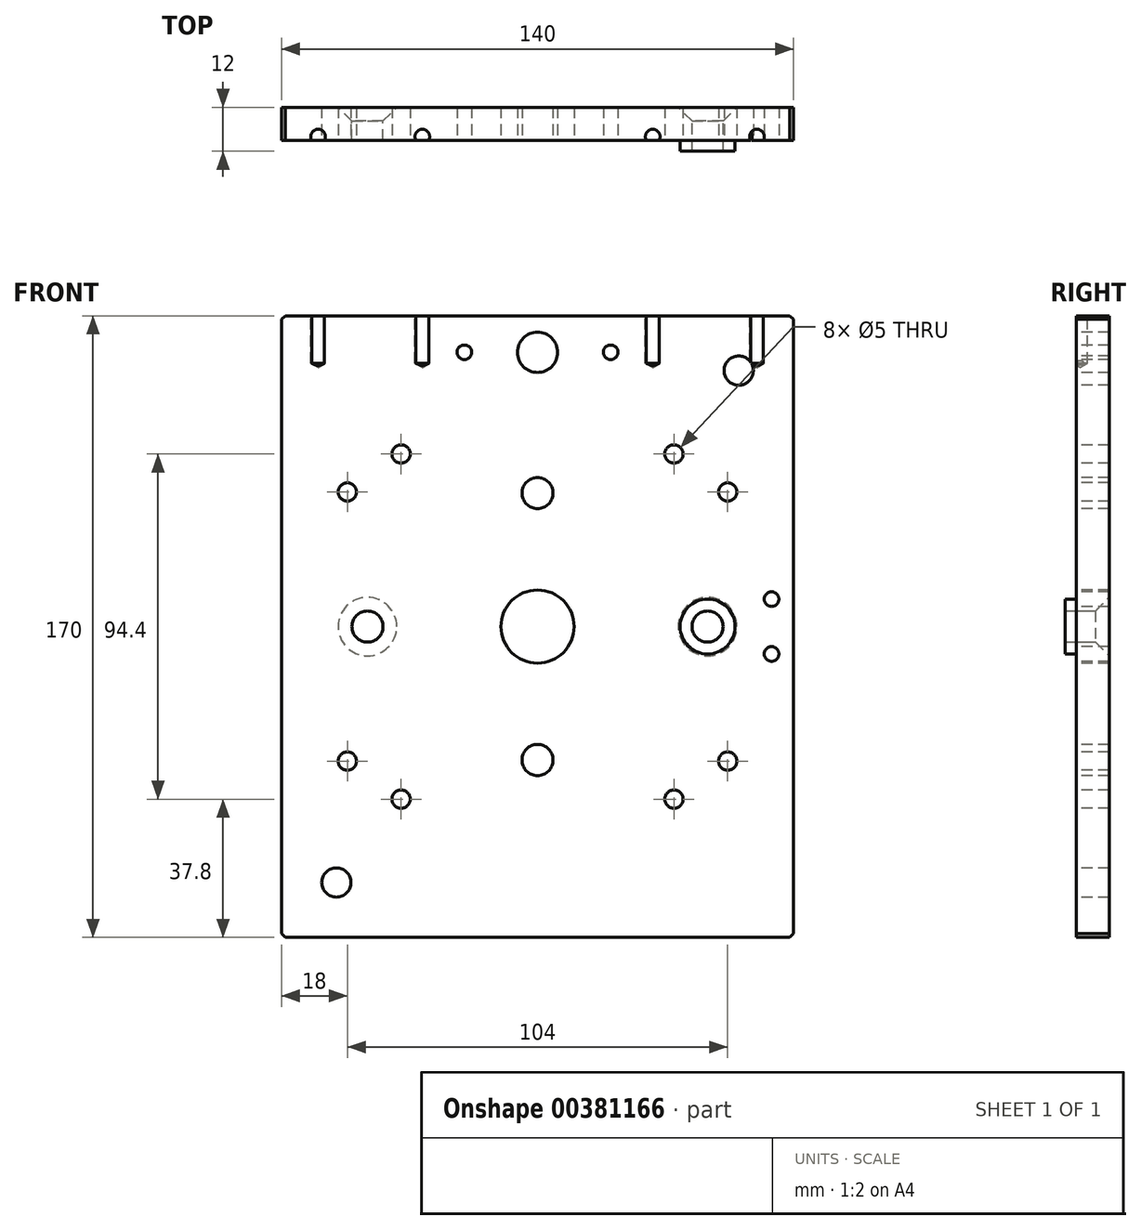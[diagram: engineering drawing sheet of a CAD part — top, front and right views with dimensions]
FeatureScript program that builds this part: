
annotation { "Feature Type Name" : "Feature", "Feature Type Description" : "" }
export const myFeature = defineFeature(function(context is Context, id is Id, definition is map)
    precondition{}
    {
        {
            var Q0;
            Q0=qCreatedBy(makeId("Front.planeOp"),FACE);
            var sketch = newSketch(context, id + "F0", { "sketchPlane" : qUnion([Q0])});
            skLineSegment(sketch, "E0.bottom", {"start": v(-70, -85) * mm, "end": v(70, -85) * mm});
            skLineSegment(sketch, "E0.top", {"start": v(-70, 85) * mm, "end": v(70, 85) * mm});
            skLineSegment(sketch, "E0.left", {"start": v(-70, -85) * mm, "end": v(-70, 85) * mm});
            skLineSegment(sketch, "E0.right", {"start": v(70, -85) * mm, "end": v(70, 85) * mm});
            skSolve(sketch);
        }
        {
            var Q0;
            Q0=makeQuery(id+"F0.imprint","IMPRINT",FACE,{"disambiguationData":[TD([[makeQuery(id+"F0.imprint","IMPRINT",EDGE,{"derivedFrom":sQuery(id+"F0.wireOp",EDGE,"E0.bottom")}),1.0]])]});
            extrude(context, id + "F1", {"entities" : qUnion([Q0]), "depth" : 12 * mm});
        }
        {
            var Q0;
            Q0=makeQuery(id+"F1.opExtrude","CAP_FACE",FACE,{"disambiguationData":[OSD([sQuery(id+"F0.wireOp",EDGE,"E0.bottom"),sQuery(id+"F0.wireOp",EDGE,"E0.top"),sQuery(id+"F0.wireOp",EDGE,"E0.left"),sQuery(id+"F0.wireOp",EDGE,"E0.right")])],"isStart":false});
            var sketch = newSketch(context, id + "F2", { "sketchPlane" : qUnion([Q0])});
            skCircle(sketch, "E1", {"center": v(0, 0) * mm, "radius": 10 * mm});
            skSolve(sketch);
        }
        {
            var Q0;
            Q0=makeQuery(id+"F2.imprint","IMPRINT",FACE,{"disambiguationData":[TD([[makeQuery(id+"F2.imprint","IMPRINT",EDGE,{"derivedFrom":sQuery(id+"F2.wireOp",EDGE,"E1")}),1.0]])]});
            extrude(context, id + "F3", {"entities" : qUnion([Q0]), "operationType" : NewBodyOperationType.REMOVE, "oppositeDirection" : true, "depth" : 12 * mm});
        }
        {
            var Q0;
            Q0=makeQuery(id+"F1.opExtrude","CAP_FACE",FACE,{"disambiguationData":[OSD([sQuery(id+"F0.wireOp",EDGE,"E0.bottom"),sQuery(id+"F0.wireOp",EDGE,"E0.top"),sQuery(id+"F0.wireOp",EDGE,"E0.left"),sQuery(id+"F0.wireOp",EDGE,"E0.right")])],"isStart":false});
            var sketch = newSketch(context, id + "F4", { "sketchPlane" : qUnion([Q0])});
            skPoint(sketch, "E2", {"position": v(-55, -70) * mm});
            skPoint(sketch, "E3", {"position": v(55, 70) * mm});
            skSolve(sketch);
        }
        {
            var Q0;
            Q0=sQuery(id+"F4.wireOp",VERTEX,"E2");
            var Q1;
            Q1=sQuery(id+"F4.wireOp",VERTEX,"E3");
            var Q2;
            Q2=makeQuery(id+"F1.opExtrude","SWEPT_BODY",BODY,{"disambiguationData":[OSD([sQuery(id+"F0.wireOp",EDGE,"E0.bottom"),sQuery(id+"F0.wireOp",EDGE,"E0.top"),sQuery(id+"F0.wireOp",EDGE,"E0.left"),sQuery(id+"F0.wireOp",EDGE,"E0.right")])]});
            hole(context, id + "F5", {"style" : HoleStyle.SIMPLE, "endStyle" : HoleEndStyle.THROUGH, "holeDiameter" : 8 * mm, "isTappedThrough" : true, "tappedDepth" : 12 * mm, "tapClearance" : 3, "locations" : qUnion([Q0, Q1]), "scope" : qUnion([Q2])});
        }
        {
            var Q0;
            Q0=makeQuery(id+"F1.opExtrude","CAP_FACE",FACE,{"disambiguationData":[OSD([sQuery(id+"F0.wireOp",EDGE,"E0.bottom"),sQuery(id+"F0.wireOp",EDGE,"E0.top"),sQuery(id+"F0.wireOp",EDGE,"E0.left"),sQuery(id+"F0.wireOp",EDGE,"E0.right")])],"isStart":false});
            var sketch = newSketch(context, id + "F6", { "sketchPlane" : qUnion([Q0])});
            skCircle(sketch, "E4", {"center": v(-46.5, 0) * mm, "radius": 7.5 * mm});
            skCircle(sketch, "E5.MirrorC", {"center": v(46.5, 0) * mm, "radius": 7.5 * mm});
            skSolve(sketch);
        }
        {
            var Q0;
            Q0=makeQuery(id+"F6.imprint","IMPRINT",FACE,{"disambiguationData":[TD([[makeQuery(id+"F6.imprint","IMPRINT",EDGE,{"derivedFrom":sQuery(id+"F6.wireOp",EDGE,"E4")}),1.0]])]});
            var Q1;
            Q1=makeQuery(id+"F6.imprint","IMPRINT",FACE,{"disambiguationData":[TD([[makeQuery(id+"F6.imprint","IMPRINT",EDGE,{"derivedFrom":sQuery(id+"F6.wireOp",EDGE,"E5.MirrorC")}),-1.0]])]});
            extrude(context, id + "F7", {"entities" : qUnion([Q0, Q1]), "operationType" : NewBodyOperationType.REMOVE, "oppositeDirection" : true, "depth" : 3 * mm});
        }
        {
            var Q0;
            Q0=makeQuery(id+"F1.opExtrude","CAP_FACE",FACE,{"disambiguationData":[OSD([sQuery(id+"F0.wireOp",EDGE,"E0.bottom"),sQuery(id+"F0.wireOp",EDGE,"E0.top"),sQuery(id+"F0.wireOp",EDGE,"E0.left"),sQuery(id+"F0.wireOp",EDGE,"E0.right")])],"isStart":true});
            var sketch = newSketch(context, id + "F8", { "sketchPlane" : qUnion([Q0])});
            skPoint(sketch, "E6", {"position": v(46.5, 0) * mm});
            skPoint(sketch, "E7.MirrorP", {"position": v(-46.5, 0) * mm});
            skSolve(sketch);
        }
        {
            var Q0;
            Q0=sQuery(id+"F8.wireOp",VERTEX,"E6");
            var Q1;
            Q1=sQuery(id+"F8.wireOp",VERTEX,"E7.MirrorP");
            var Q2;
            Q2=makeQuery(id+"F1.opExtrude","SWEPT_BODY",BODY,{"disambiguationData":[OSD([sQuery(id+"F0.wireOp",EDGE,"E0.bottom"),sQuery(id+"F0.wireOp",EDGE,"E0.top"),sQuery(id+"F0.wireOp",EDGE,"E0.left"),sQuery(id+"F0.wireOp",EDGE,"E0.right")])]});
            hole(context, id + "F9", {"style" : HoleStyle.C_SINK, "endStyle" : HoleEndStyle.BLIND, "holeDiameter" : 8.5 * mm, "cSinkDiameter" : 16 * mm, "cSinkAngle" : 90 * degree, "holeDepth" : 12 * mm, "isTappedThrough" : true, "tappedDepth" : 12 * mm, "tapClearance" : 3, "locations" : qUnion([Q0, Q1]), "scope" : qUnion([Q2])});
        }
        {
            var Q0;
            Q0=makeQuery(id+"F1.opExtrude","CAP_FACE",FACE,{"disambiguationData":[OSD([sQuery(id+"F0.wireOp",EDGE,"E0.bottom"),sQuery(id+"F0.wireOp",EDGE,"E0.top"),sQuery(id+"F0.wireOp",EDGE,"E0.left"),sQuery(id+"F0.wireOp",EDGE,"E0.right")])],"isStart":false});
            var sketch = newSketch(context, id + "F10", { "sketchPlane" : qUnion([Q0])});
            skPoint(sketch, "E8", {"position": v(0, -36.5) * mm});
            skPoint(sketch, "E9.MirrorP", {"position": v(0, 36.5) * mm});
            skSolve(sketch);
        }
        {
            var Q0;
            Q0=sQuery(id+"F10.wireOp",VERTEX,"E8");
            var Q1;
            Q1=sQuery(id+"F10.wireOp",VERTEX,"E9.MirrorP");
            var Q2;
            Q2=makeQuery(id+"F1.opExtrude","SWEPT_BODY",BODY,{"disambiguationData":[OSD([sQuery(id+"F0.wireOp",EDGE,"E0.bottom"),sQuery(id+"F0.wireOp",EDGE,"E0.top"),sQuery(id+"F0.wireOp",EDGE,"E0.left"),sQuery(id+"F0.wireOp",EDGE,"E0.right")])]});
            hole(context, id + "F11", {"style" : HoleStyle.SIMPLE, "endStyle" : HoleEndStyle.THROUGH, "standardTappedOrClearance" : lookupTablePath({ "standard" : "ISO", "engagement" : "75%", "pitch" : "1.5 mm", "size" : "M10", "type" : "Tapped" }), "standardBlindInLast" : lookupTablePath({ "standard" : "ISO", "engagement" : "75%", "pitch" : "1.5 mm", "size" : "M10", "type" : "Tapped" }), "holeDiameter" : 8.5 * mm, "showTappedDepth" : true, "isTappedThrough" : true, "tappedDepth" : 12 * mm, "tapClearance" : 3, "locations" : qUnion([Q0, Q1]), "scope" : qUnion([Q2]), "majorDiameter" : 10 * mm});
        }
        {
            var Q0;
            Q0=makeQuery(id+"F1.opExtrude","CAP_FACE",FACE,{"disambiguationData":[OSD([sQuery(id+"F0.wireOp",EDGE,"E0.bottom"),sQuery(id+"F0.wireOp",EDGE,"E0.top"),sQuery(id+"F0.wireOp",EDGE,"E0.left"),sQuery(id+"F0.wireOp",EDGE,"E0.right")])],"isStart":false});
            var sketch = newSketch(context, id + "F12", { "sketchPlane" : qUnion([Q0])});
            skPoint(sketch, "E10", {"position": v(-52, 36.8) * mm});
            skPoint(sketch, "E11", {"position": v(-37.3, 47.2) * mm});
            skPoint(sketch, "E12.MirrorP", {"position": v(52, 36.8) * mm});
            skPoint(sketch, "E13.MirrorP", {"position": v(37.3, 47.2) * mm});
            skPoint(sketch, "E14.MirrorP", {"position": v(52, -36.8) * mm});
            skPoint(sketch, "E15.MirrorP", {"position": v(37.3, -47.2) * mm});
            skPoint(sketch, "E16.MirrorP", {"position": v(-37.3, -47.2) * mm});
            skPoint(sketch, "E17.MirrorP", {"position": v(-52, -36.8) * mm});
            skSolve(sketch);
        }
        {
            var Q0;
            Q0=sQuery(id+"F12.wireOp",VERTEX,"E14.MirrorP");
            var Q1;
            Q1=sQuery(id+"F12.wireOp",VERTEX,"E15.MirrorP");
            var Q2;
            Q2=sQuery(id+"F12.wireOp",VERTEX,"E16.MirrorP");
            var Q3;
            Q3=sQuery(id+"F12.wireOp",VERTEX,"E17.MirrorP");
            var Q4;
            Q4=sQuery(id+"F12.wireOp",VERTEX,"E10");
            var Q5;
            Q5=sQuery(id+"F12.wireOp",VERTEX,"E11");
            var Q6;
            Q6=sQuery(id+"F12.wireOp",VERTEX,"E13.MirrorP");
            var Q7;
            Q7=sQuery(id+"F12.wireOp",VERTEX,"E12.MirrorP");
            var Q8;
            Q8=makeQuery(id+"F1.opExtrude","SWEPT_BODY",BODY,{"disambiguationData":[OSD([sQuery(id+"F0.wireOp",EDGE,"E0.bottom"),sQuery(id+"F0.wireOp",EDGE,"E0.top"),sQuery(id+"F0.wireOp",EDGE,"E0.left"),sQuery(id+"F0.wireOp",EDGE,"E0.right")])]});
            hole(context, id + "F13", {"style" : HoleStyle.SIMPLE, "endStyle" : HoleEndStyle.THROUGH, "standardTappedOrClearance" : lookupTablePath({ "standard" : "ISO", "engagement" : "75%", "pitch" : "1 mm", "size" : "M6", "type" : "Tapped" }), "standardBlindInLast" : lookupTablePath({ "standard" : "ISO", "engagement" : "75%", "pitch" : "1 mm", "size" : "M6", "type" : "Tapped" }), "holeDiameter" : 5 * mm, "showTappedDepth" : true, "isTappedThrough" : true, "tappedDepth" : 12 * mm, "tapClearance" : 3, "locations" : qUnion([Q0, Q1, Q2, Q3, Q4, Q5, Q6, Q7]), "scope" : qUnion([Q8]), "majorDiameter" : 6 * mm});
        }
        {
            var Q0;
            Q0=makeQuery(id+"F1.opExtrude","CAP_FACE",FACE,{"disambiguationData":[OSD([sQuery(id+"F0.wireOp",EDGE,"E0.bottom"),sQuery(id+"F0.wireOp",EDGE,"E0.top"),sQuery(id+"F0.wireOp",EDGE,"E0.left"),sQuery(id+"F0.wireOp",EDGE,"E0.right")])],"isStart":false});
            var sketch = newSketch(context, id + "F14", { "sketchPlane" : qUnion([Q0])});
            skPoint(sketch, "E18", {"position": v(64, -7.5) * mm});
            skPoint(sketch, "E19.MirrorP", {"position": v(64, 7.5) * mm});
            skPoint(sketch, "E20", {"position": v(-20, 75) * mm});
            skPoint(sketch, "E21.MirrorP", {"position": v(20, 75) * mm});
            skSolve(sketch);
        }
        {
            var Q0;
            Q0=sQuery(id+"F14.wireOp",VERTEX,"E20");
            var Q1;
            Q1=sQuery(id+"F14.wireOp",VERTEX,"E21.MirrorP");
            var Q2;
            Q2=sQuery(id+"F14.wireOp",VERTEX,"E19.MirrorP");
            var Q3;
            Q3=sQuery(id+"F14.wireOp",VERTEX,"E18");
            var Q4;
            Q4=makeQuery(id+"F1.opExtrude","SWEPT_BODY",BODY,{"disambiguationData":[OSD([sQuery(id+"F0.wireOp",EDGE,"E0.bottom"),sQuery(id+"F0.wireOp",EDGE,"E0.top"),sQuery(id+"F0.wireOp",EDGE,"E0.left"),sQuery(id+"F0.wireOp",EDGE,"E0.right")])]});
            hole(context, id + "F15", {"style" : HoleStyle.SIMPLE, "endStyle" : HoleEndStyle.THROUGH, "standardTappedOrClearance" : lookupTablePath({ "standard" : "ISO", "engagement" : "75%", "pitch" : "1 mm", "size" : "M5", "type" : "Tapped" }), "standardBlindInLast" : lookupTablePath({ "standard" : "ISO", "engagement" : "75%", "pitch" : "1 mm", "size" : "M5", "type" : "Tapped" }), "holeDiameter" : 4 * mm, "showTappedDepth" : true, "isTappedThrough" : true, "tappedDepth" : 12 * mm, "tapClearance" : 3, "locations" : qUnion([Q0, Q1, Q2, Q3]), "scope" : qUnion([Q4])});
        }
        {
            var Q0;
            Q0=makeQuery(id+"F1.opExtrude","CAP_FACE",FACE,{"disambiguationData":[OSD([sQuery(id+"F0.wireOp",EDGE,"E0.bottom"),sQuery(id+"F0.wireOp",EDGE,"E0.top"),sQuery(id+"F0.wireOp",EDGE,"E0.left"),sQuery(id+"F0.wireOp",EDGE,"E0.right")])],"isStart":false});
            var sketch = newSketch(context, id + "F16", { "sketchPlane" : qUnion([Q0])});
            skCircle(sketch, "E22", {"center": v(0, 75) * mm, "radius": 5.5 * mm});
            skSolve(sketch);
        }
        {
            var Q0;
            Q0=makeQuery(id+"F16.imprint","IMPRINT",FACE,{"disambiguationData":[TD([[makeQuery(id+"F16.imprint","IMPRINT",EDGE,{"derivedFrom":sQuery(id+"F16.wireOp",EDGE,"E22")}),1.0]])]});
            extrude(context, id + "F17", {"entities" : qUnion([Q0]), "operationType" : NewBodyOperationType.REMOVE, "oppositeDirection" : true, "depth" : 12 * mm});
        }
        {
            var Q0;
            Q0=makeQuery(id+"F1.opExtrude","SWEPT_FACE",FACE,{"disambiguationData":[OSD([sQuery(id+"F0.wireOp",EDGE,"E0.top")])]});
            var sketch = newSketch(context, id + "F18", { "sketchPlane" : qUnion([Q0])});
            skPoint(sketch, "E23", {"position": v(60, -8) * mm});
            skPoint(sketch, "E24", {"position": v(31.5, -8) * mm});
            skPoint(sketch, "E25.MirrorP", {"position": v(-31.5, -8) * mm});
            skPoint(sketch, "E26.MirrorP", {"position": v(-60, -8) * mm});
            skSolve(sketch);
        }
        {
            var Q0;
            Q0=sQuery(id+"F18.wireOp",VERTEX,"E23");
            var Q1;
            Q1=sQuery(id+"F18.wireOp",VERTEX,"E24");
            var Q2;
            Q2=sQuery(id+"F18.wireOp",VERTEX,"E25.MirrorP");
            var Q3;
            Q3=sQuery(id+"F18.wireOp",VERTEX,"E26.MirrorP");
            var Q4;
            Q4=makeQuery(id+"F1.opExtrude","SWEPT_BODY",BODY,{"disambiguationData":[OSD([sQuery(id+"F0.wireOp",EDGE,"E0.bottom"),sQuery(id+"F0.wireOp",EDGE,"E0.top"),sQuery(id+"F0.wireOp",EDGE,"E0.left"),sQuery(id+"F0.wireOp",EDGE,"E0.right")])]});
            hole(context, id + "F19", {"style" : HoleStyle.SIMPLE, "endStyle" : HoleEndStyle.BLIND, "standardTappedOrClearance" : lookupTablePath({ "standard" : "ISO", "engagement" : "75%", "pitch" : "1 mm", "size" : "M5", "type" : "Tapped" }), "standardBlindInLast" : lookupTablePath({ "standard" : "ISO", "engagement" : "75%", "pitch" : "1 mm", "size" : "M5", "type" : "Tapped" }), "holeDiameter" : 4 * mm, "showTappedDepth" : true, "holeDepth" : 13 * mm, "isTappedThrough" : true, "tappedDepth" : 10 * mm, "tapClearance" : 3, "locations" : qUnion([Q0, Q1, Q2, Q3]), "scope" : qUnion([Q4])});
        }
        {
            var Q0;
            Q0=makeQuery(id+"F1.opExtrude","SWEPT_EDGE",EDGE,{"disambiguationData":[OSD([sQuery(id+"F0.wireOp",EDGE,"E0.bottom"),sQuery(id+"F0.wireOp",EDGE,"E0.left")])]});
            var Q1;
            Q1=makeQuery(id+"F1.opExtrude","SWEPT_EDGE",EDGE,{"disambiguationData":[OSD([sQuery(id+"F0.wireOp",EDGE,"E0.top"),sQuery(id+"F0.wireOp",EDGE,"E0.left")])]});
            var Q2;
            Q2=makeQuery(id+"F1.opExtrude","SWEPT_EDGE",EDGE,{"disambiguationData":[OSD([sQuery(id+"F0.wireOp",EDGE,"E0.top"),sQuery(id+"F0.wireOp",EDGE,"E0.right")])]});
            var Q3;
            Q3=makeQuery(id+"F1.opExtrude","SWEPT_EDGE",EDGE,{"disambiguationData":[OSD([sQuery(id+"F0.wireOp",EDGE,"E0.bottom"),sQuery(id+"F0.wireOp",EDGE,"E0.right")])]});
            chamfer(context, id + "F20", {"entities" : qUnion([Q0, Q1, Q2, Q3]), "width" : 1 * mm, "tangentPropagation" : true});
        }
    });
